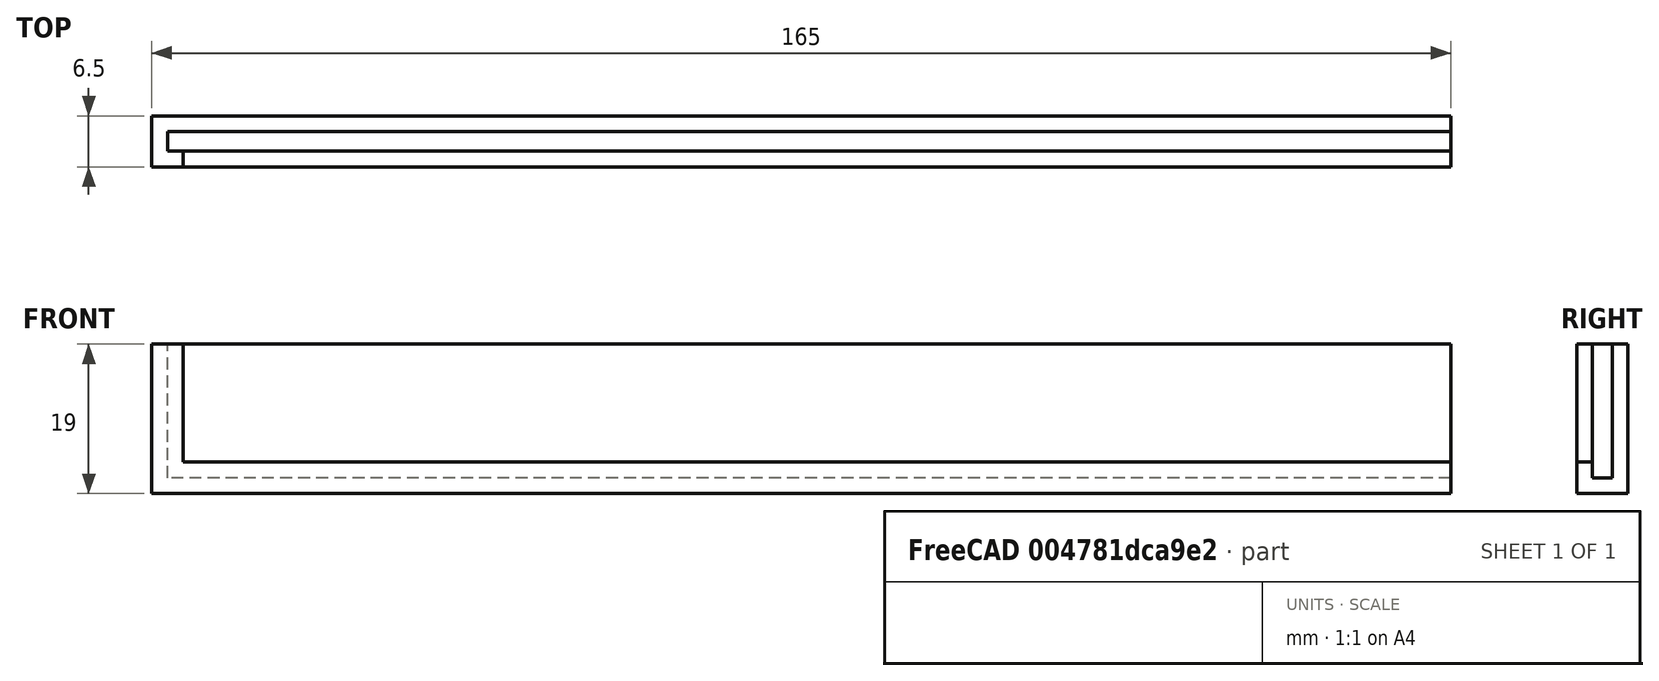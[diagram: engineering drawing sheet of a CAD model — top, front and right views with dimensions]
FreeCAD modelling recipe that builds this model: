
FCSTD DOCUMENT  (FreeCAD 0.18.4R)
Label: Tukortarto
License: All rights reserved
LicenseURL: http://en.wikipedia.org/wiki/All_rights_reserved
objects: Part::Box×3, Part::Cut×2, Part::Mirroring×1
note: 6 computed .brp shape members not serialized (recipe doc carries the construction recipe); baked Part::Feature solids carry a one-line shape summary decoded from their .brp

FEATURE [Part::Box] Box001  label="Cube001"
  AttacherType = Attacher::AttachEngine3D
  Height = 17
  Length = 163
  Placement = pos=(0,2,2) rot=(0,0,1;0rad)
  Width = 2.5
FEATURE [Part::Box] Box002  label="Cube002"
  AttacherType = Attacher::AttachEngine3D
  Height = 15
  Length = 161
  Placement = pos=(0,0,4) rot=(0,0,1;0rad)
  Width = 2
FEATURE [Part::Box] Box  label="Cube"
  AttacherType = Attacher::AttachEngine3D
  Height = 19
  Length = 165
  Width = 6.5
FEATURE [Part::Cut] Cut
  Base = -> Box
  Tool = -> Box001
FEATURE [Part::Cut] Cut001
  Base = -> Cut
  Tool = -> Box002
FEATURE [Part::Mirroring] Part__Mirroring  label="Cut001 (Mirror #1)"
  Base = (0,0,0)
  Normal = (0,0,1)
  Placement = pos=(0,0,0) rot=(0,1,0;3.14159rad)
  Source = -> Cut001
